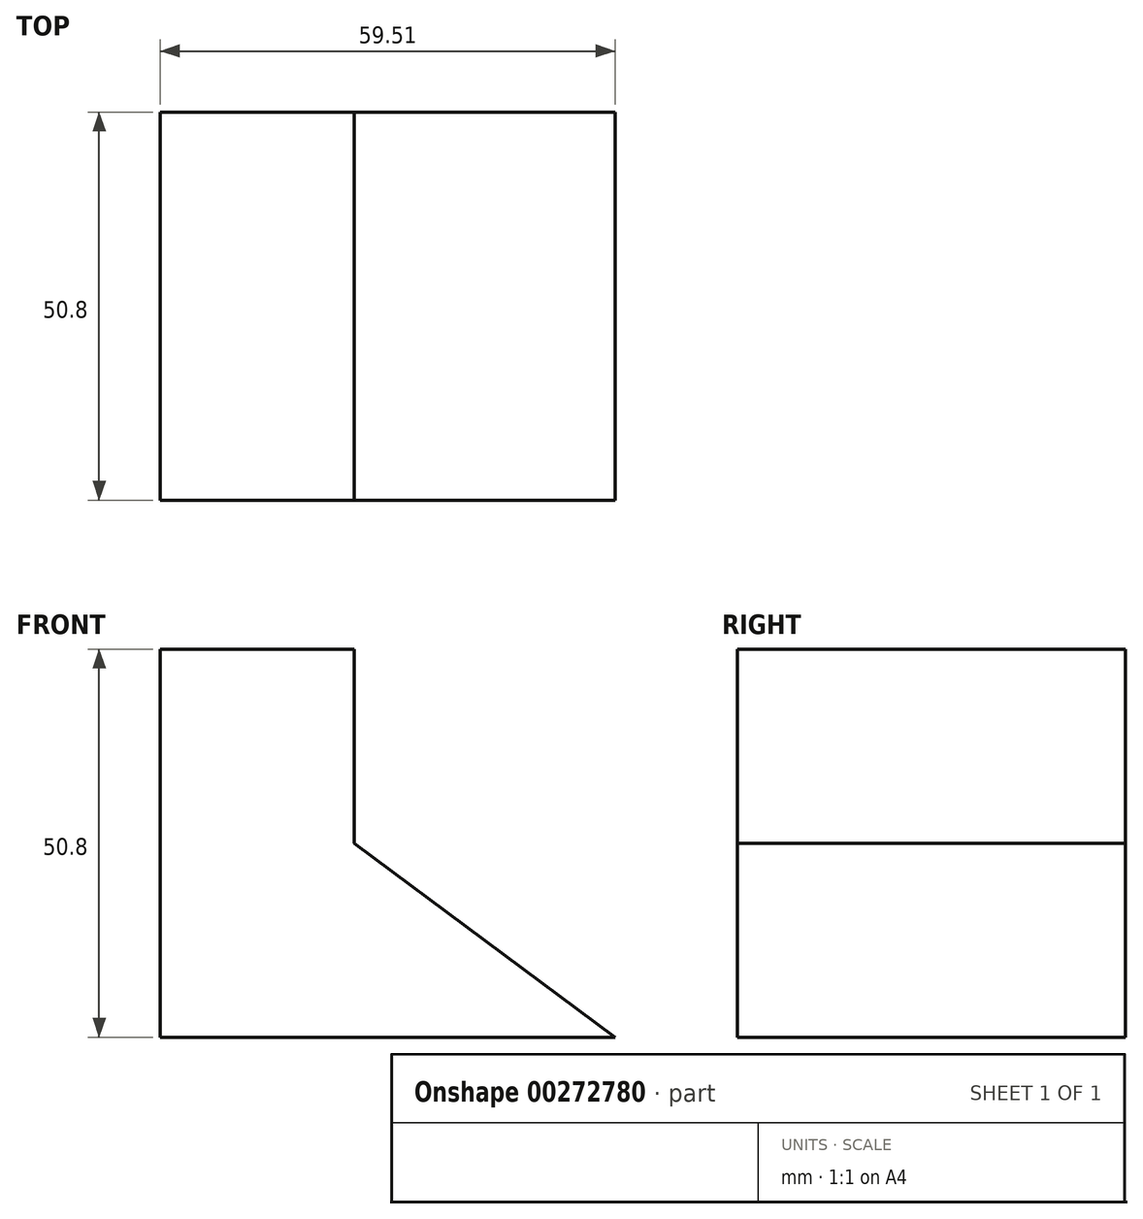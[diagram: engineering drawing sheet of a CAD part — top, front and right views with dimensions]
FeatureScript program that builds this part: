
annotation { "Feature Type Name" : "Feature", "Feature Type Description" : "" }
export const myFeature = defineFeature(function(context is Context, id is Id, definition is map)
    precondition{}
    {
        {
            var Q0;
            Q0=qCreatedBy(makeId("Front.planeOp"),FACE);
            var sketch = newSketch(context, id + "F0", { "sketchPlane" : qUnion([Q0])});
            skLineSegment(sketch, "E0", {"start": v(-64.68, 0) * mm, "end": v(-64.68, 50.8) * mm});
            skLineSegment(sketch, "E1", {"start": v(-64.68, 50.8) * mm, "end": v(-39.28, 50.8) * mm});
            skLineSegment(sketch, "E2", {"start": v(-39.28, 50.8) * mm, "end": v(-39.28, 25.4) * mm});
            skLineSegment(sketch, "E3", {"start": v(-64.68, 0) * mm, "end": v(-5.17, 0) * mm});
            skLineSegment(sketch, "E4", {"start": v(-39.28, 25.4) * mm, "end": v(-5.17, 0) * mm});
            skSolve(sketch);
        }
        {
            var Q0;
            Q0 = qSketchRegion(id + "F0", true);
            extrude(context, id + "F1", {"entities" : qUnion([Q0]), "depth" : 50.8 * mm});
        }
    });
